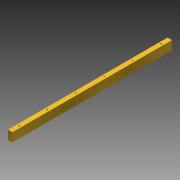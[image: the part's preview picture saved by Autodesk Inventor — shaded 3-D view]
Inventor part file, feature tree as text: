
AUTODESK INVENTOR PART (.ipt)
format: ipt  version: 2016 (Build 200138000, 138)  size: 119,808 bytes
history: native  units: in
note: dims shown in document units (in); Inventor stores cm internally (conversion verified against a paired STEP export)
features: sketch x3, hole x3, pattern_linear x2, extrude x1
ambient origin geometry x8: Origin, YZ Plane, XZ Plane, XY Plane, X Axis, Y Axis, Z Axis, Center Point
bodies: Solid1 (feature_tree)
feature tree (9):
  extrude  "Extrusion1"  Depth=0.5in
  sketch  "Sketch3"  dims[d6=9.0in d7=0.0in d8=0.3703in]
  hole  "Hole1"  [1 undecoded]
  pattern_linear  "Rectangular Pattern1"  Count1=4 Spacing1=1.0in
  hole  "Hole5"  [1 undecoded]
  hole  "Hole6"  [1 undecoded]
  pattern_linear  "Rectangular Pattern5"  Spacing1=0.5in  [1 undecoded]
  sketch  "Sketch2"  dims[d3=0.25in d5=0.5in]
  sketch  "Sketch7"  dims[d9=0.7in d10=0.067in d11=0.75in d12=0.375in d13=0.25in d14=0.5635in d15=1.0in d16=0.8108in d17=1.5748in d19=1.0in d60=8.2in d61=0.3703in d62=0.067in d63=0.75in d64=0.375in d65=0.25in d66=0.5635in d67=1.0in d68=0.8108in d69=0.5in d70=0.125in d71=0.067in d72=0.75in d73=0.375in d74=0.25in d75=0.5635in d76=0.25in d77=0.8108in d78=2.3622in d80=1.6in]
note: 4 required parameter values undecoded (feature->parameter linkage not recoverable at this tier; creation-order binding heuristic only, values carry confidence <= 0.55)
